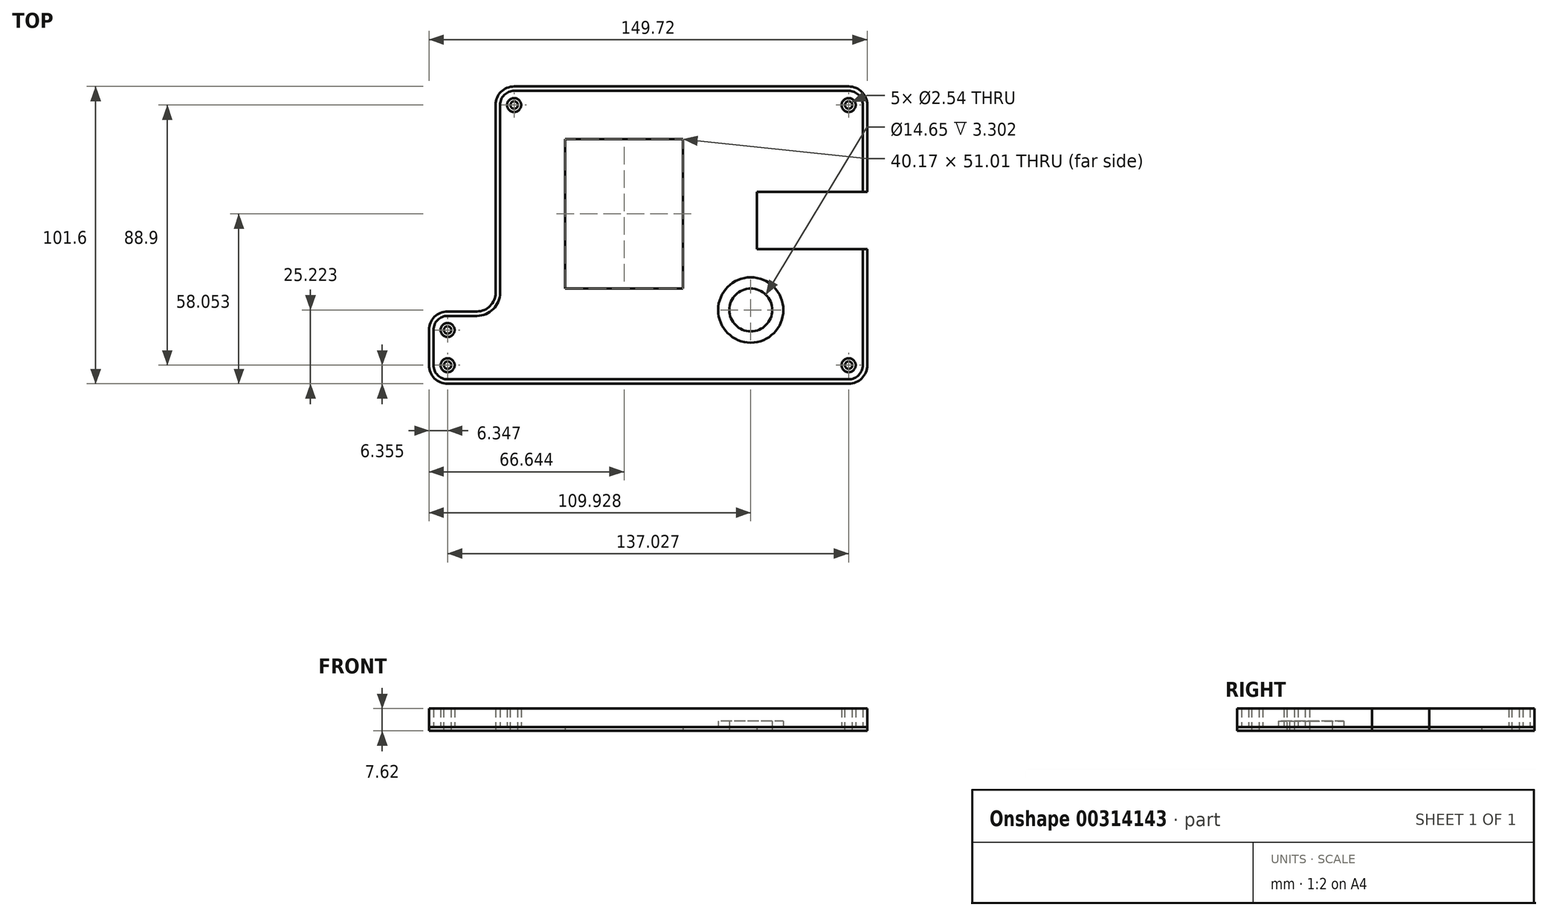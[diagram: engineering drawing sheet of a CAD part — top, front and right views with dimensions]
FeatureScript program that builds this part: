
annotation { "Feature Type Name" : "Feature", "Feature Type Description" : "" }
export const myFeature = defineFeature(function(context is Context, id is Id, definition is map)
    precondition{}
    {
        {
            var Q0;
            Q0=qCreatedBy(makeId("Top.planeOp"),FACE);
            var sketch = newSketch(context, id + "F0", { "sketchPlane" : qUnion([Q0])});
            skLineSegment(sketch, "E0.bottom", {"start": v(4.64, 5.22) * mm, "end": v(125.3, 5.22) * mm});
            skLineSegment(sketch, "E0.top", {"start": v(11, 106.82) * mm, "end": v(125.3, 106.82) * mm});
            skLineSegment(sketch, "E0.left", {"start": v(4.64, 36.3) * mm, "end": v(4.64, 100.47) * mm});
            skLineSegment(sketch, "E0.right", {"start": v(131.64, 11.57) * mm, "end": v(131.64, 51.28) * mm});
            skLineSegment(sketch, "E1", {"start": v(4.64, 5.22) * mm, "end": v(-11.73, 5.22) * mm});
            skLineSegment(sketch, "E2", {"start": v(-18.08, 11.57) * mm, "end": v(-18.08, 23.6) * mm});
            skLineSegment(sketch, "E3", {"start": v(-11.73, 29.95) * mm, "end": v(-1.7, 29.95) * mm});
            skLineSegment(sketch, "E4", {"start": v(131.64, 70.83) * mm, "end": v(93.88, 70.83) * mm});
            skLineSegment(sketch, "E5", {"start": v(93.88, 70.83) * mm, "end": v(93.88, 51.28) * mm});
            skLineSegment(sketch, "E6", {"start": v(93.88, 51.28) * mm, "end": v(131.64, 51.28) * mm});
            skLineSegment(sketch, "E7.trimOffspring", {"start": v(131.64, 70.83) * mm, "end": v(131.64, 100.47) * mm});
            skPoint(sketch, "E8.visualSharp", {"position": v(4.64, 29.95) * mm});
            skArc(sketch, "E8.filletArc", {"start": v(-0.55, 30.06) * mm, "mid": v(3.18, 32.24) * mm, "end": v(4.64, 36.3) * mm});
            skPoint(sketch, "E9.visualSharp", {"position": v(-1.7, 29.95) * mm});
            skArc(sketch, "E9.filletArc", {"start": v(-1.7, 29.95) * mm, "mid": v(-1.12, 29.98) * mm, "end": v(-0.55, 30.06) * mm});
            skPoint(sketch, "E10.visualSharp", {"position": v(-18.08, 29.95) * mm});
            skArc(sketch, "E10.filletArc", {"start": v(-11.73, 29.95) * mm, "mid": v(-16.22, 28.09) * mm, "end": v(-18.08, 23.6) * mm});
            skPoint(sketch, "E11.visualSharp", {"position": v(-18.08, 5.22) * mm});
            skArc(sketch, "E11.filletArc", {"start": v(-18.08, 11.57) * mm, "mid": v(-16.22, 7.08) * mm, "end": v(-11.73, 5.22) * mm});
            skPoint(sketch, "E12.visualSharp", {"position": v(4.64, 106.82) * mm});
            skArc(sketch, "E12.filletArc", {"start": v(11, 106.82) * mm, "mid": v(6.5, 104.96) * mm, "end": v(4.64, 100.47) * mm});
            skPoint(sketch, "E13.visualSharp", {"position": v(131.64, 106.82) * mm});
            skArc(sketch, "E13.filletArc", {"start": v(131.64, 100.47) * mm, "mid": v(129.78, 104.96) * mm, "end": v(125.3, 106.82) * mm});
            skPoint(sketch, "E14.visualSharp", {"position": v(131.64, 5.22) * mm});
            skArc(sketch, "E14.filletArc", {"start": v(125.3, 5.22) * mm, "mid": v(129.78, 7.08) * mm, "end": v(131.64, 11.57) * mm});
            skLineSegment(sketch, "E15.bottom", {"start": v(28.48, 88.78) * mm, "end": v(68.65, 88.78) * mm});
            skLineSegment(sketch, "E15.top", {"start": v(28.48, 37.77) * mm, "end": v(68.65, 37.77) * mm});
            skLineSegment(sketch, "E15.left", {"start": v(28.48, 88.78) * mm, "end": v(28.48, 37.77) * mm});
            skLineSegment(sketch, "E15.right", {"start": v(68.65, 88.78) * mm, "end": v(68.65, 37.77) * mm});
            skSolve(sketch);
        }
        {
            var Q0;
            Q0 = qSketchRegion(id + "F0", true);
            extrude(context, id + "F1", {"entities" : qUnion([Q0]), "depth" : 1.27 * mm});
        }
        {
            var Q0;
            Q0=makeQuery(id+"F1.opExtrude","CAP_FACE",FACE,{"disambiguationData":[OSD([sQuery(id+"F0.wireOp",EDGE,"E0.bottom"),sQuery(id+"F0.wireOp",EDGE,"E0.top"),sQuery(id+"F0.wireOp",EDGE,"E0.left"),sQuery(id+"F0.wireOp",EDGE,"E0.right"),sQuery(id+"F0.wireOp",EDGE,"E1"),sQuery(id+"F0.wireOp",EDGE,"E2"),sQuery(id+"F0.wireOp",EDGE,"E3"),sQuery(id+"F0.wireOp",EDGE,"E4"),sQuery(id+"F0.wireOp",EDGE,"E5"),sQuery(id+"F0.wireOp",EDGE,"E6"),sQuery(id+"F0.wireOp",EDGE,"E7.trimOffspring"),sQuery(id+"F0.wireOp",EDGE,"E8.filletArc"),sQuery(id+"F0.wireOp",EDGE,"E9.filletArc"),sQuery(id+"F0.wireOp",EDGE,"E10.filletArc"),sQuery(id+"F0.wireOp",EDGE,"E11.filletArc"),sQuery(id+"F0.wireOp",EDGE,"E12.filletArc"),sQuery(id+"F0.wireOp",EDGE,"E13.filletArc"),sQuery(id+"F0.wireOp",EDGE,"E14.filletArc"),sQuery(id+"F0.wireOp",EDGE,"E15.bottom"),sQuery(id+"F0.wireOp",EDGE,"E15.top"),sQuery(id+"F0.wireOp",EDGE,"E15.left"),sQuery(id+"F0.wireOp",EDGE,"E15.right")])],"isStart":false});
            var sketch = newSketch(context, id + "F2", { "sketchPlane" : qUnion([Q0])});
            skLineSegment(sketch, "E16.0", {"start": v(130.12, 11.57) * mm, "end": v(130.12, 51.28) * mm});
            skArc(sketch, "E16.1", {"start": v(125.3, 6.75) * mm, "mid": v(128.7, 8.16) * mm, "end": v(130.12, 11.57) * mm});
            skLineSegment(sketch, "E16.2", {"start": v(125.3, 6.75) * mm, "end": v(-11.73, 6.75) * mm});
            skArc(sketch, "E16.3", {"start": v(11, 105.3) * mm, "mid": v(7.58, 103.89) * mm, "end": v(6.17, 100.47) * mm});
            skLineSegment(sketch, "E16.4", {"start": v(11, 105.3) * mm, "end": v(125.3, 105.3) * mm});
            skArc(sketch, "E16.5", {"start": v(130.12, 100.47) * mm, "mid": v(128.7, 103.89) * mm, "end": v(125.3, 105.3) * mm});
            skLineSegment(sketch, "E16.6", {"start": v(130.12, 70.83) * mm, "end": v(130.12, 100.47) * mm});
            skLineSegment(sketch, "E16.7", {"start": v(6.17, 36.3) * mm, "end": v(6.17, 100.47) * mm});
            skArc(sketch, "E16.8", {"start": v(-1.7, 28.43) * mm, "mid": v(3.86, 30.73) * mm, "end": v(6.17, 36.3) * mm});
            skLineSegment(sketch, "E16.9", {"start": v(-11.73, 28.43) * mm, "end": v(-1.7, 28.43) * mm});
            skArc(sketch, "E16.10", {"start": v(-11.73, 28.43) * mm, "mid": v(-15.15, 27.01) * mm, "end": v(-16.56, 23.6) * mm});
            skLineSegment(sketch, "E16.11", {"start": v(-16.56, 11.57) * mm, "end": v(-16.56, 23.6) * mm});
            skArc(sketch, "E16.12", {"start": v(-16.56, 11.57) * mm, "mid": v(-15.15, 8.16) * mm, "end": v(-11.73, 6.75) * mm});
            skPoint(sketch, "E17.0", {"position": v(11, 106.82) * mm});
            skLineSegment(sketch, "E18.0", {"start": v(11, 106.82) * mm, "end": v(125.3, 106.82) * mm});
            skPoint(sketch, "E19.0", {"position": v(129.78, 104.96) * mm});
            skLineSegment(sketch, "E20.0", {"start": v(131.64, 70.83) * mm, "end": v(131.64, 100.47) * mm});
            skLineSegment(sketch, "E21.0", {"start": v(131.64, 11.57) * mm, "end": v(131.64, 51.28) * mm});
            skPoint(sketch, "E22.0", {"position": v(129.78, 7.08) * mm});
            skLineSegment(sketch, "E23.0", {"start": v(125.3, 5.22) * mm, "end": v(-11.73, 5.22) * mm});
            skArc(sketch, "E24.0", {"start": v(125.3, 5.22) * mm, "mid": v(129.78, 7.08) * mm, "end": v(131.64, 11.57) * mm});
            skPoint(sketch, "E25.0", {"position": v(-16.22, 7.08) * mm});
            skPoint(sketch, "E26.0", {"position": v(-18.08, 17.59) * mm});
            skPoint(sketch, "E27.0", {"position": v(-16.22, 28.09) * mm});
            skLineSegment(sketch, "E28.0", {"start": v(-11.73, 29.95) * mm, "end": v(-1.7, 29.95) * mm});
            skArc(sketch, "E29.0", {"start": v(-1.7, 29.95) * mm, "mid": v(2.78, 31.8) * mm, "end": v(4.64, 36.3) * mm});
            skLineSegment(sketch, "E30.0", {"start": v(4.64, 36.3) * mm, "end": v(4.64, 100.47) * mm});
            skLineSegment(sketch, "E31", {"start": v(130.12, 70.83) * mm, "end": v(131.64, 70.83) * mm});
            skLineSegment(sketch, "E32", {"start": v(131.64, 51.28) * mm, "end": v(130.12, 51.28) * mm});
            skArc(sketch, "E33.0", {"start": v(-11.73, 29.95) * mm, "mid": v(-16.22, 28.09) * mm, "end": v(-18.08, 23.6) * mm});
            skLineSegment(sketch, "E34.0", {"start": v(-18.08, 11.57) * mm, "end": v(-18.08, 23.6) * mm});
            skArc(sketch, "E35.0", {"start": v(131.64, 100.47) * mm, "mid": v(129.78, 104.96) * mm, "end": v(125.3, 106.82) * mm});
            skSolve(sketch);
        }
        {
            var Q0;
            Q0 = qSketchRegion(id + "F2", true);
            var Q1;
            Q1=makeQuery(id+"F2.imprint","IMPRINT",FACE,{"disambiguationData":[TD([[makeQuery(id+"F2.imprint","IMPRINT",EDGE,{"derivedFrom":sQuery(id+"F2.wireOp",EDGE,"E16.0")}),-1.0]])]});
            extrude(context, id + "F3", {"entities" : qUnion([Q0, Q1]), "depth" : 6.35 * mm});
        }
        {
            var Q0;
            Q0=makeQuery(id+"F1.opExtrude","CAP_FACE",FACE,{"disambiguationData":[OSD([sQuery(id+"F0.wireOp",EDGE,"E0.bottom"),sQuery(id+"F0.wireOp",EDGE,"E0.top"),sQuery(id+"F0.wireOp",EDGE,"E0.left"),sQuery(id+"F0.wireOp",EDGE,"E0.right"),sQuery(id+"F0.wireOp",EDGE,"E1"),sQuery(id+"F0.wireOp",EDGE,"E2"),sQuery(id+"F0.wireOp",EDGE,"E3"),sQuery(id+"F0.wireOp",EDGE,"E4"),sQuery(id+"F0.wireOp",EDGE,"E5"),sQuery(id+"F0.wireOp",EDGE,"E6"),sQuery(id+"F0.wireOp",EDGE,"E7.trimOffspring"),sQuery(id+"F0.wireOp",EDGE,"E8.filletArc"),sQuery(id+"F0.wireOp",EDGE,"E9.filletArc"),sQuery(id+"F0.wireOp",EDGE,"E10.filletArc"),sQuery(id+"F0.wireOp",EDGE,"E11.filletArc"),sQuery(id+"F0.wireOp",EDGE,"E12.filletArc"),sQuery(id+"F0.wireOp",EDGE,"E13.filletArc"),sQuery(id+"F0.wireOp",EDGE,"E14.filletArc"),sQuery(id+"F0.wireOp",EDGE,"E15.bottom"),sQuery(id+"F0.wireOp",EDGE,"E15.top"),sQuery(id+"F0.wireOp",EDGE,"E15.left"),sQuery(id+"F0.wireOp",EDGE,"E15.right")])],"isStart":false});
            var sketch = newSketch(context, id + "F4", { "sketchPlane" : qUnion([Q0])});
            skCircle(sketch, "E36", {"center": v(11, 100.47) * mm, "radius": 2.39 * mm});
            skCircle(sketch, "E37", {"center": v(125.3, 100.47) * mm, "radius": 2.39 * mm});
            skCircle(sketch, "E38", {"center": v(125.3, 11.57) * mm, "radius": 2.39 * mm});
            skCircle(sketch, "E39", {"center": v(-11.73, 23.6) * mm, "radius": 2.39 * mm});
            skCircle(sketch, "E40", {"center": v(-11.73, 11.57) * mm, "radius": 2.39 * mm});
            skSolve(sketch);
        }
        {
            var Q0;
            Q0 = qSketchRegion(id + "F4", true);
            extrude(context, id + "F5", {"entities" : qUnion([Q0]), "operationType" : NewBodyOperationType.ADD, "depth" : 6.35 * mm});
        }
        {
            var Q0;
            Q0=makeQuery(id+"F5.opExtrude","CAP_FACE",FACE,{"disambiguationData":[OSD([sQuery(id+"F4.wireOp",EDGE,"E36")])],"isStart":false});
            var sketch = newSketch(context, id + "F6", { "sketchPlane" : qUnion([Q0])});
            skCircle(sketch, "E41", {"center": v(11, 100.47) * mm, "radius": 1.27 * mm});
            skCircle(sketch, "E42", {"center": v(-11.73, 23.6) * mm, "radius": 1.27 * mm});
            skCircle(sketch, "E43", {"center": v(-11.73, 11.57) * mm, "radius": 1.27 * mm});
            skCircle(sketch, "E44", {"center": v(125.3, 11.57) * mm, "radius": 1.27 * mm});
            skCircle(sketch, "E45", {"center": v(125.3, 100.47) * mm, "radius": 1.27 * mm});
            skSolve(sketch);
        }
        {
            var Q0;
            Q0 = qSketchRegion(id + "F6", true);
            extrude(context, id + "F7", {"entities" : qUnion([Q0]), "operationType" : NewBodyOperationType.REMOVE, "endBound" : BoundingType.THROUGH_ALL, "oppositeDirection" : true, "depth" : 25.4 * mm});
        }
        {
            var Q0;
            Q0=makeQuery(id+"F1.opExtrude","CAP_FACE",FACE,{"disambiguationData":[OSD([sQuery(id+"F0.wireOp",EDGE,"E0.bottom"),sQuery(id+"F0.wireOp",EDGE,"E0.top"),sQuery(id+"F0.wireOp",EDGE,"E0.left"),sQuery(id+"F0.wireOp",EDGE,"E0.right"),sQuery(id+"F0.wireOp",EDGE,"E1"),sQuery(id+"F0.wireOp",EDGE,"E2"),sQuery(id+"F0.wireOp",EDGE,"E3"),sQuery(id+"F0.wireOp",EDGE,"E4"),sQuery(id+"F0.wireOp",EDGE,"E5"),sQuery(id+"F0.wireOp",EDGE,"E6"),sQuery(id+"F0.wireOp",EDGE,"E7.trimOffspring"),sQuery(id+"F0.wireOp",EDGE,"E8.filletArc"),sQuery(id+"F0.wireOp",EDGE,"E9.filletArc"),sQuery(id+"F0.wireOp",EDGE,"E10.filletArc"),sQuery(id+"F0.wireOp",EDGE,"E11.filletArc"),sQuery(id+"F0.wireOp",EDGE,"E12.filletArc"),sQuery(id+"F0.wireOp",EDGE,"E13.filletArc"),sQuery(id+"F0.wireOp",EDGE,"E14.filletArc"),sQuery(id+"F0.wireOp",EDGE,"E15.bottom"),sQuery(id+"F0.wireOp",EDGE,"E15.top"),sQuery(id+"F0.wireOp",EDGE,"E15.left"),sQuery(id+"F0.wireOp",EDGE,"E15.right")])],"isStart":false});
            var sketch = newSketch(context, id + "F8", { "sketchPlane" : qUnion([Q0])});
            skCircle(sketch, "E46", {"center": v(91.85, 30.44) * mm, "radius": 11.15 * mm});
            skCircle(sketch, "E47", {"center": v(91.85, 30.44) * mm, "radius": 7.33 * mm});
            skSolve(sketch);
        }
        {
            var Q0;
            Q0 = qSketchRegion(id + "F8", true);
            extrude(context, id + "F9", {"entities" : qUnion([Q0]), "operationType" : NewBodyOperationType.ADD, "depth" : 2.03 * mm});
        }
        {
            var Q0;
            Q0=makeQuery(id+"F9.boolean.opBoolean","SPLIT",FACE,{"disambiguationData":[TD([makeQuery(id+"F9.opExtrude","SWEPT_FACE",FACE,{"disambiguationData":[OSD([sQuery(id+"F8.wireOp",EDGE,"E47")])]})])],"derivedFrom":makeQuery(id+"F1.opExtrude","CAP_FACE",FACE,{"disambiguationData":[OSD([sQuery(id+"F0.wireOp",EDGE,"E0.bottom"),sQuery(id+"F0.wireOp",EDGE,"E0.top"),sQuery(id+"F0.wireOp",EDGE,"E0.left"),sQuery(id+"F0.wireOp",EDGE,"E0.right"),sQuery(id+"F0.wireOp",EDGE,"E1"),sQuery(id+"F0.wireOp",EDGE,"E2"),sQuery(id+"F0.wireOp",EDGE,"E3"),sQuery(id+"F0.wireOp",EDGE,"E4"),sQuery(id+"F0.wireOp",EDGE,"E5"),sQuery(id+"F0.wireOp",EDGE,"E6"),sQuery(id+"F0.wireOp",EDGE,"E7.trimOffspring"),sQuery(id+"F0.wireOp",EDGE,"E8.filletArc"),sQuery(id+"F0.wireOp",EDGE,"E9.filletArc"),sQuery(id+"F0.wireOp",EDGE,"E10.filletArc"),sQuery(id+"F0.wireOp",EDGE,"E11.filletArc"),sQuery(id+"F0.wireOp",EDGE,"E12.filletArc"),sQuery(id+"F0.wireOp",EDGE,"E13.filletArc"),sQuery(id+"F0.wireOp",EDGE,"E14.filletArc"),sQuery(id+"F0.wireOp",EDGE,"E15.bottom"),sQuery(id+"F0.wireOp",EDGE,"E15.top"),sQuery(id+"F0.wireOp",EDGE,"E15.left"),sQuery(id+"F0.wireOp",EDGE,"E15.right")])],"isStart":false})});
            var sketch = newSketch(context, id + "F10", { "sketchPlane" : qUnion([Q0])});
            skCircle(sketch, "E48.0", {"center": v(91.85, 30.44) * mm, "radius": 7.33 * mm});
            skSolve(sketch);
        }
        {
            var Q0;
            Q0 = qSketchRegion(id + "F10", true);
            extrude(context, id + "F11", {"entities" : qUnion([Q0]), "operationType" : NewBodyOperationType.REMOVE, "endBound" : BoundingType.THROUGH_ALL, "oppositeDirection" : true, "depth" : 25.4 * mm});
        }
    });
